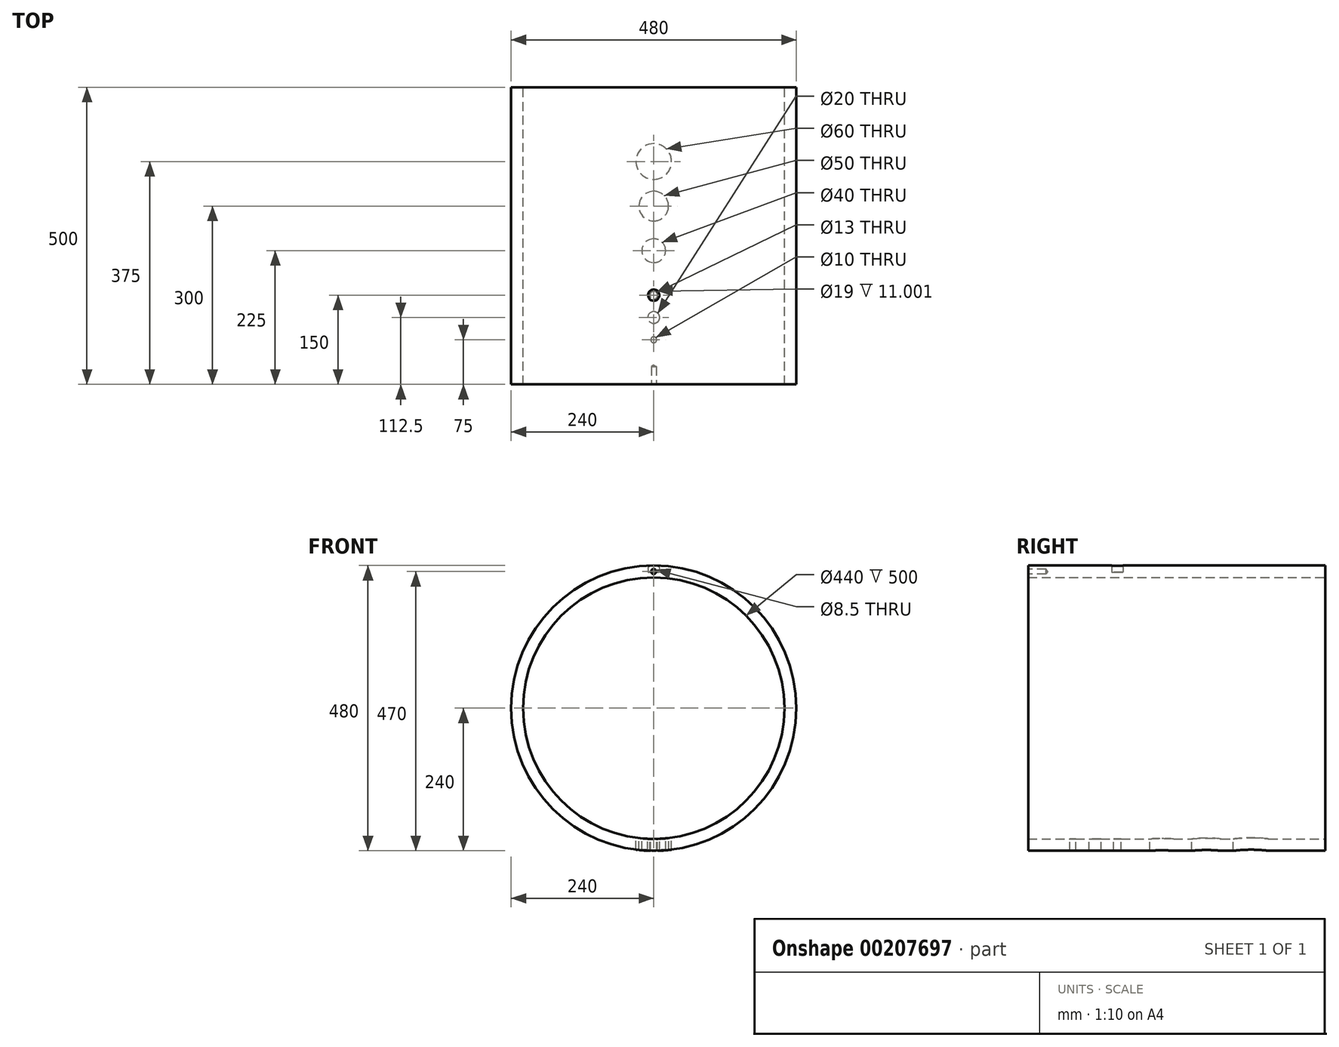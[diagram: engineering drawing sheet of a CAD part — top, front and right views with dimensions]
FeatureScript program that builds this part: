
annotation { "Feature Type Name" : "Feature", "Feature Type Description" : "" }
export const myFeature = defineFeature(function(context is Context, id is Id, definition is map)
    precondition{}
    {
        {
            var Q0;
            Q0=qCreatedBy(makeId("Front.planeOp"),FACE);
            var sketch = newSketch(context, id + "F0", { "sketchPlane" : qUnion([Q0])});
            skCircle(sketch, "E0", {"center": v(0, 0) * mm, "radius": 240 * mm});
            skCircle(sketch, "E1", {"center": v(0, 0) * mm, "radius": 220 * mm});
            skSolve(sketch);
        }
        {
            var Q0;
            Q0=makeQuery(id+"F0.imprint","IMPRINT",FACE,{"disambiguationData":[TD([[makeQuery(id+"F0.imprint","IMPRINT",EDGE,{"derivedFrom":sQuery(id+"F0.wireOp",EDGE,"E0")}),1.0]])]});
            extrude(context, id + "F1", {"entities" : qUnion([Q0]), "endBound" : BoundingType.SYMMETRIC, "depth" : 500 * mm});
        }
        {
            var Q0;
            Q0=makeQuery(id+"F1.opExtrude","CAP_FACE",FACE,{"disambiguationData":[OSD([sQuery(id+"F0.wireOp",EDGE,"E0"),sQuery(id+"F0.wireOp",EDGE,"E1")])],"isStart":false});
            var sketch = newSketch(context, id + "F2", { "sketchPlane" : qUnion([Q0])});
            skCircle(sketch, "E2", {"center": v(0, 230) * mm, "radius": 5 * mm});
            skSolve(sketch);
        }
        {
            var Q0;
            Q0=sQuery(id+"F2.wireOp",VERTEX,"E2.center");
            var Q1;
            Q1=makeQuery(id+"F1.opExtrude","SWEPT_BODY",BODY,{"disambiguationData":[OSD([sQuery(id+"F0.wireOp",EDGE,"E0"),sQuery(id+"F0.wireOp",EDGE,"E1")])]});
            hole(context, id + "F3", {"style" : HoleStyle.SIMPLE, "endStyle" : HoleEndStyle.BLIND, "standardTappedOrClearance" : lookupTablePath({ "standard" : "ISO", "engagement" : "75%", "pitch" : "1.5 mm", "size" : "M10", "type" : "Tapped" }), "standardBlindInLast" : lookupTablePath({ "standard" : "ISO", "engagement" : "75%", "pitch" : "1.5 mm", "size" : "M10", "type" : "Tapped" }), "holeDiameter" : 8.5 * mm, "showTappedDepth" : true, "holeDepth" : 30 * mm, "tappedDepth" : 25.5 * mm, "tapClearance" : 3, "locations" : qUnion([Q0]), "scope" : qUnion([Q1]), "majorDiameter" : 10 * mm});
        }
        {
            var Q0;
            Q0=qCreatedBy(makeId("Top.planeOp"),FACE);
            var sketch = newSketch(context, id + "F4", { "sketchPlane" : qUnion([Q0])});
            skCircle(sketch, "E3", {"center": v(0, -175) * mm, "radius": 5 * mm});
            skCircle(sketch, "E4", {"center": v(0, -100) * mm, "radius": 6.5 * mm});
            skCircle(sketch, "E5", {"center": v(0, -25) * mm, "radius": 20 * mm});
            skCircle(sketch, "E6", {"center": v(0, 50) * mm, "radius": 25 * mm});
            skCircle(sketch, "E7", {"center": v(0, 125) * mm, "radius": 30 * mm});
            skCircle(sketch, "E8", {"center": v(0, -137.5) * mm, "radius": 10 * mm});
            skSolve(sketch);
        }
        {
            var Q0;
            Q0 = qSketchRegion(id + "F4", true);
            extrude(context, id + "F5", {"entities" : qUnion([Q0]), "operationType" : NewBodyOperationType.REMOVE, "endBound" : BoundingType.THROUGH_ALL, "oppositeDirection" : true, "depth" : 500 * mm});
        }
        {
            var Q0;
            Q0=qCreatedBy(makeId("Top.planeOp"),FACE);
            var sketch = newSketch(context, id + "F6", { "sketchPlane" : qUnion([Q0])});
            skCircle(sketch, "E9", {"center": v(0, -100) * mm, "radius": 9.5 * mm});
            skSolve(sketch);
        }
        {
            var Q0;
            Q0 = qSketchRegion(id + "F6", true);
            extrude(context, id + "F7", {"entities" : qUnion([Q0]), "operationType" : NewBodyOperationType.REMOVE, "depth" : 240 * mm, "hasSecondDirection" : true, "secondDirectionOppositeDirection" : false, "secondDirectionDepth" : (240 - 11) * mm});
        }
    });
